# Revit family: i-PRO-5MP-Outdoor-Dome-Network Camera-WV-S2552L
name_source: partatom
category: Security Devices
units: mm (PartAtom-declared; Revit-internal decimal feet)

## family parameters
Cut with Voids When Loaded = No
Host = Face
Maintain Annotation Orientation = No
OmniClass Number = 23.85.10.14.11
OmniClass Title = Cameras
Part Type = Normal
Room Calculation Point = No
Round Connector Dimension = Use Diameter
Shared = No

## types (2) — shared parameters
Angle Of View = 103
Audio In = Yes
Audio Out = Yes
Communication Ports = 10Base-T / 100Base-TX, RJ45 connector
Date Last Modified = 2024/03/11
Day Or Night = Yes
Description = i-PRO, 5MP, Outdoor, Dome Network Camera, WV-S2552L
Diameter = 6.063 "
EMC = FCC (Part15 ClassA), ICES-003 ClassA, EN55032 ClassA, EN55035
Equipment Abbreviation = SC
Family Version = 1.0.0
HFOV Max 169 = 103.00°
HFOV Max 43 = 103.00°
HFOV Min 169 = 33.00°
HFOV Min 43 = 33.00°
Height = 4.134 "
IP Or Analog = IP
Indoor Or Outdoor = Outdoor
Manufacturer = i-PRO Co., Ltd.
Minimum Illumination = 0.070 lx
Model = WV-S2552L
Model Disclaimer = Contact i-PRO for more information
Operational Humidity = 10 to 100 % (no condensation)
Operational Temperature = -30 °C to +60 °C (-22 °F to 140 °F)
Pan Max = 166.00°
Pan Min = -194.00°
Part Description = i-PRO, 5MP, Outdoor, Dome Network Camera, WV-S2552L
Part Number = WV-S2552L
Product Documentation Link = https://i-pro.com
Product Material = Paint -i-Pro White
Product Page URL = https://i-pro.com
Provide Feedback = https://i-pro.com
Saftey = UL (UL62368-1), c-UL (CSA C22.2 No.62368-1), CE, IEC62368-1
Shock Resistance = 50J (IEC 60068-2-75 compliant), IK10 (IEC62262))
Storage Temperature = -40 °C to +60 °C (-40 °F to 140 °F)
Tilt Max = 85.00°
Tilt Min = -30.00°
URL = https://i-pro.com
VFOV Max 169 = 55.00°
VFOV Max 43 = 55.00°
VFOV Min 169 = 19.00°
VFOV Min 43 = 25.00°
Water and Dust Resistance = IIP66 (IEC60529), Type 4X(UL50E), NEMA 4X compliant
Wind Resistance = Up to 40 m/s {approx. 89 mph}
Yaw Max = 100.00°
Yaw Min = -100.00°
z Base Radius = 3.031 "
z Camera Type = 25500
z Const Pan Handle Length = 19.488 "
z Const Tilt Base Length = 9.843 "
z Const Tilt Base2 Length = 19.685 "
z Const Tilt Handle Length = 11.811 "
z Const Yaw Base Length = 10.236 "
z Const Yaw Base2 Length = 17.323 "
z Const Yaw Handle Length = 9.252 "
z Dome Radius = 1.654 "
z VV Viewpoint Depth Max = 1.283 "
z VV Viewpoint Depth Min = 1.283 "
zero-valued in all types: Default Elevation

## type names (no varying parameters)
- WV-S2552L (Wall)
- WV-S2552L (Ceiling)

## geometry (parser evidence)
native form markers: Blend x4, Sweep x10
no freeform markers — native parametric forms only
